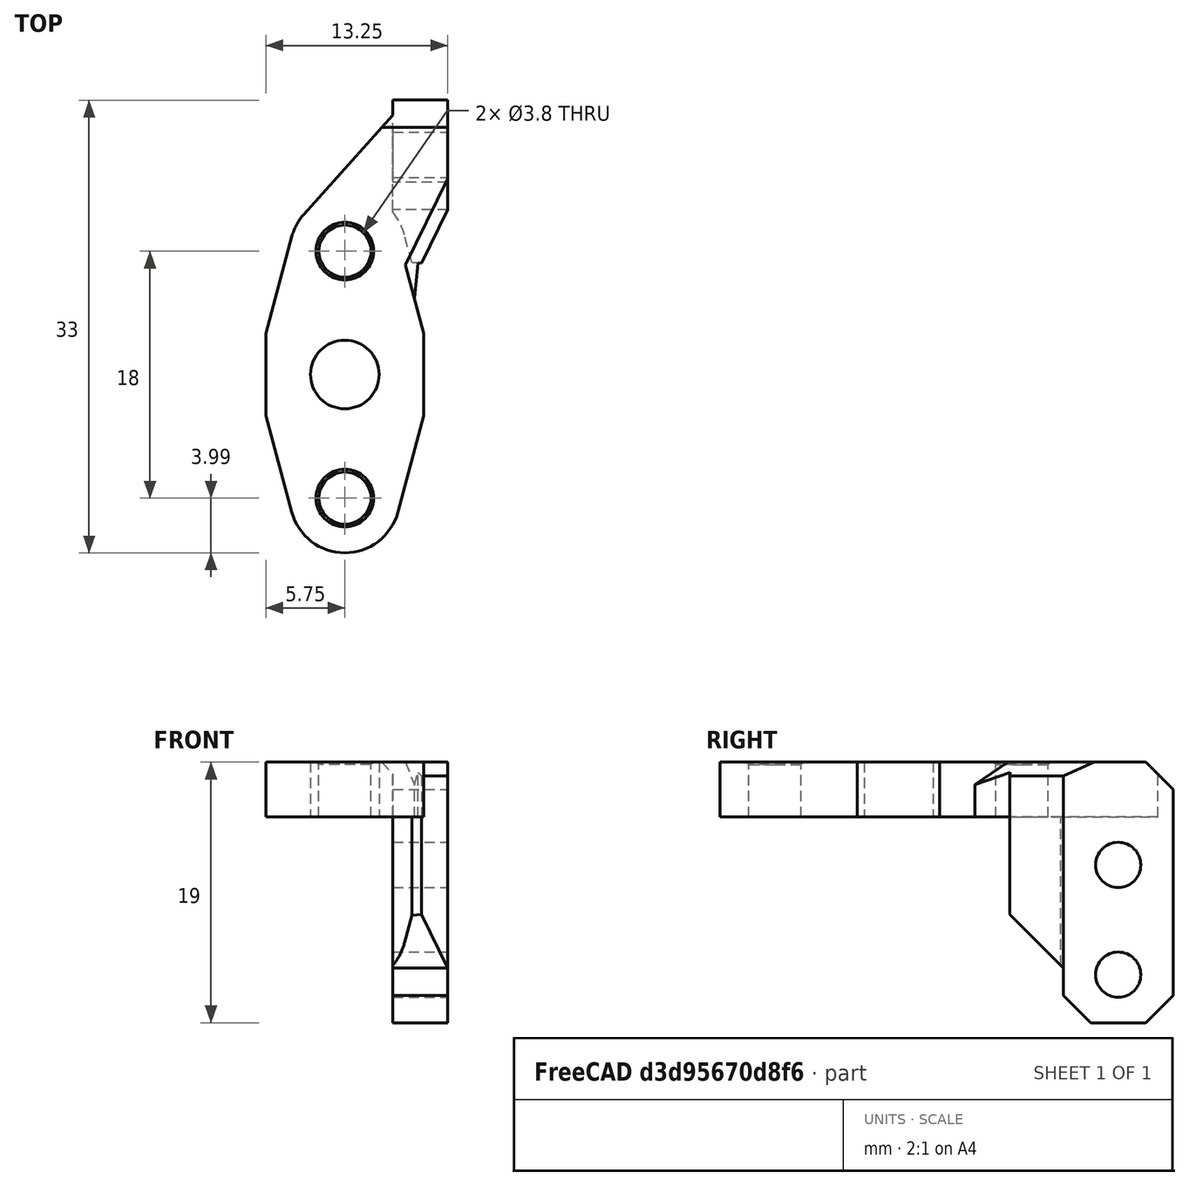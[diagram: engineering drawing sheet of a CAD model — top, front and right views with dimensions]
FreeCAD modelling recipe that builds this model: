
FCSTD DOCUMENT  (FreeCAD 0.19R24291 (Git))
Label: bltouch-mount-thread-insert-mod
License: Other
LicenseURL: GPL3
objects: Part::Cylinder×2, Part::Feature×1, Part::MultiFuse×1, Part::Cut×1, Part::Chamfer×1
note: 6 computed .brp shape members not serialized (recipe doc carries the construction recipe); baked Part::Feature solids carry a one-line shape summary decoded from their .brp

FEATURE [Part::Feature] Part__Feature112001111  label="bl_touch_mount001"
  Placement = pos=(27.9058,21.1435,0.21127) rot=(0,0,1;0rad)
  shape: bbox 13.25 x 33 x 19 mm, 31 faces (baked)
FEATURE [Part::Cylinder] Cylinder
  Angle = 360
  AttacherType = Attacher::AttachEngine3D
  Height = 10
  Placement = pos=(-0.09,9.13,0) rot=(0,0,1;0rad)
  Radius = 1.9
FEATURE [Part::Cylinder] Cylinder001
  Angle = 360
  AttacherType = Attacher::AttachEngine3D
  Height = 10
  Placement = pos=(-0.09,-8.87,0) rot=(0,0,1;0rad)
  Radius = 1.9
FEATURE [Part::MultiFuse] Fusion
  Shapes = -> [Cylinder,Cylinder001]
FEATURE [Part::Cut] Cut
  Base = -> Part__Feature112001111
  Tool = -> Fusion
FEATURE [Part::Chamfer] Chamfer
  Base = -> Cut
  Edges = 2 edges r=0.2: [Edge79,Edge83]
